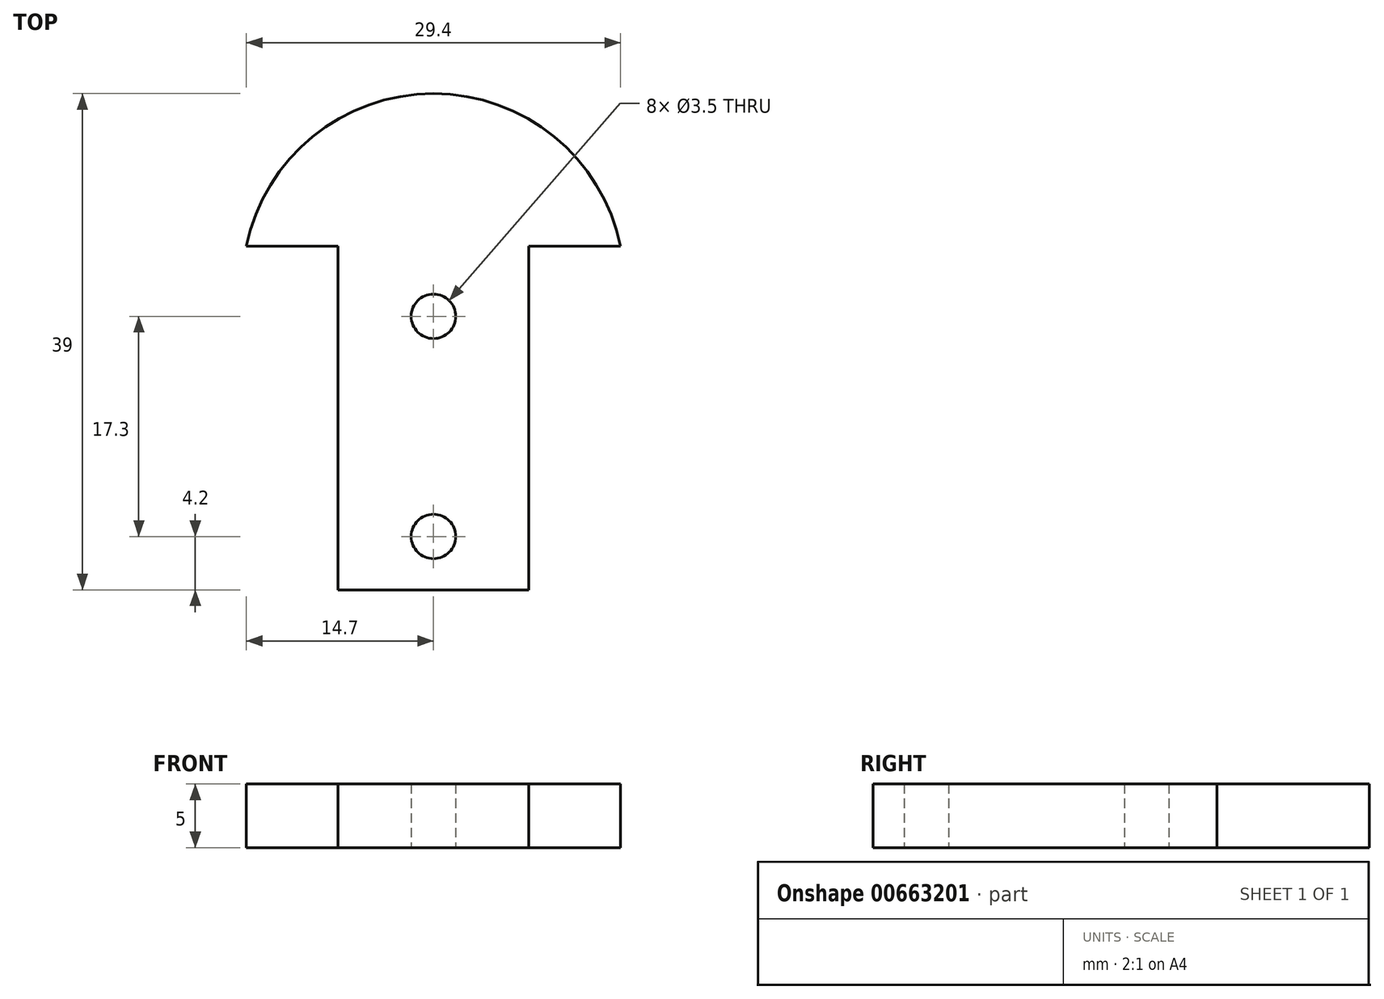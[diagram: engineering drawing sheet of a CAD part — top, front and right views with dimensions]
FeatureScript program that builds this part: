
annotation { "Feature Type Name" : "Feature", "Feature Type Description" : "" }
export const myFeature = defineFeature(function(context is Context, id is Id, definition is map)
    precondition{}
    {
        {
            var Q0;
            Q0=qCreatedBy(makeId("Top.planeOp"),FACE);
            var sketch = newSketch(context, id + "F0", { "sketchPlane" : qUnion([Q0])});
            skLineSegment(sketch, "E0.top", {"start": v(-7.5, -13.5) * mm, "end": v(7.5, -13.5) * mm});
            skLineSegment(sketch, "E0.left", {"start": v(-7.5, 13.5) * mm, "end": v(-7.5, -13.5) * mm});
            skLineSegment(sketch, "E0.right", {"start": v(7.5, 13.5) * mm, "end": v(7.5, -13.5) * mm});
            skPoint(sketch, "E0.middle", {"position": v(0, 0) * mm});
            skLineSegment(sketch, "E1", {"start": v(-7.5, 13.5) * mm, "end": v(-14.7, 13.5) * mm});
            skLineSegment(sketch, "E2", {"start": v(7.5, 13.5) * mm, "end": v(14.7, 13.5) * mm});
            skArc(sketch, "E3", {"start": v(14.7, 13.5) * mm, "mid": v(0, 25.5) * mm, "end": v(-14.7, 13.5) * mm});
            skCircle(sketch, "E4", {"center": v(0, -9.3) * mm, "radius": 1.75 * mm});
            skCircle(sketch, "E5", {"center": v(0, 8) * mm, "radius": 1.75 * mm});
            skSolve(sketch);
        }
        {
            var Q0;
            Q0 = qSketchRegion(id + "F0", true);
            extrude(context, id + "F1", {"entities" : qUnion([Q0]), "depth" : 5 * mm, "offsetDistance" : 25 * mm});
        }
    });
